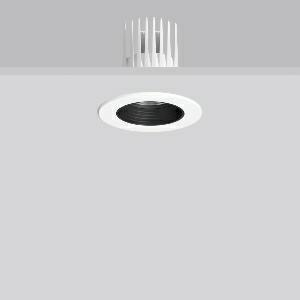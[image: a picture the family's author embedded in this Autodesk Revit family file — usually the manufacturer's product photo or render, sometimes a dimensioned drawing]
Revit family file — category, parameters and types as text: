
# Revit family: heledon_mini_e_901744_002_76_0368
name_source: partatom
category: Lighting Fixtures
units: mm (PartAtom-declared; Revit-internal decimal feet)

## family parameters
Cut with Voids When Loaded = No
Host = Face
Light Source = No
Part Type = Normal
Room Calculation Point = No
Round Connector Dimension = Use Diameter
Shared = No

## types (1)
- HELEDON mini E (1 x LED Modul 930, 2100 lm, 3000)
    Apparent Load = 20 VA
    Approval mark = CE
    CIE Flux Codes = 96 100 100 100 100
    Color Rendering = 90
    Color Temperature = 3000
    Default Elevation = 1800 mm
    Description = Series: HELEDON mini
Round recessed downlight. Housing: die-cast aluminium, powder-coated. Black plastic ring and recessed LED to prevent glare from the side. Optical assembly with lens made of plastic (polycarbonate) for the best homogeneous light distribution - can be changed without tools. Best colour rendering index Ra>90. Suitable for Recessed ceiling mounting. Installation without tools thanks to spring fastening system. Including separate LED converter with connecting cable 600 mm.High quality converter without flickering and stroboscopic effect. Through-wiring box (5 pole) available as accessory. The following accessories can be mounted without use of tools: interchangeable lenses, decorative glasses, honeycomb louvre, clear and frosted diffusers, white interchangeable plastic ring. 
Colour: traffic white, matt (RAL 9016)
Diameter: 124 mm
Height: 3 mm
Cut-out diameter: 114 mm
Recess height: 170 mm
Luminaire: recess height: 120 mm
Lamp: LED
Socket: without socket
Colour temperature: 3000K
Colour rendering index (CRI): 92
System power: 20 W
Rated luminous flux: 2100 lm
Luminous efficiency: 105 lm/W
Control gear: Converter, dimmable, DALI
Protection class: II
Type of protection: IP 20
    Height = 0 mm  [stored 0 ft]
    Lamp = 1 x LED Modul 930
    Lamp Light Flux = 2100 lm
    Lamp count = 1
    Length = 124 mm  [stored 0.406824 ft]
    Lifetime = 50000 h
    Luminous efficacy = 105 lm/W
    Manufacturer = RZB
    ModVariant = No
    Model = 901744.002.76
    Mounting Place = Ceiling
    Mounting Type = Recessed
    Number of Poles = 1
    OnlyDefault = Yes
    Power Factor = 1
    Product Name = HELEDON mini E
    Product group = Recessed downlights
    ProductGroupID = 402
    Protection Class = Protection class II
    Protection Degree = IP 20
    RLX_Detail_Level = 1
    RLX_Emergency_Light_Flux = 0 lm
    RLX_Emergency_Type = 0
    RLX_Emergency_Type_DB = No
    RlxData = <blob elided: 126801 chars, md5=244426ff>
    Socket = socket
    Standby Power = 0 W
    System Light Flux = 2100 lm
    System Power = 20 W
    Type Comments = Product without accessories
    Type Image = 901656.002.jpg
    URL = http://relux.com
    VarID = ---
    Voltage = 230 V
    Voltage Range = 220-240 V
    Weight = 0.00 kg
    Width = 0 mm  [stored 0 ft]

note: [stored X ft] marks values corroborated as IEEE doubles in the binary element streams (Revit-internal decimal feet)

## geometry (parser evidence)
native form markers: Blend x4, Sweep x12
no freeform markers — native parametric forms only
